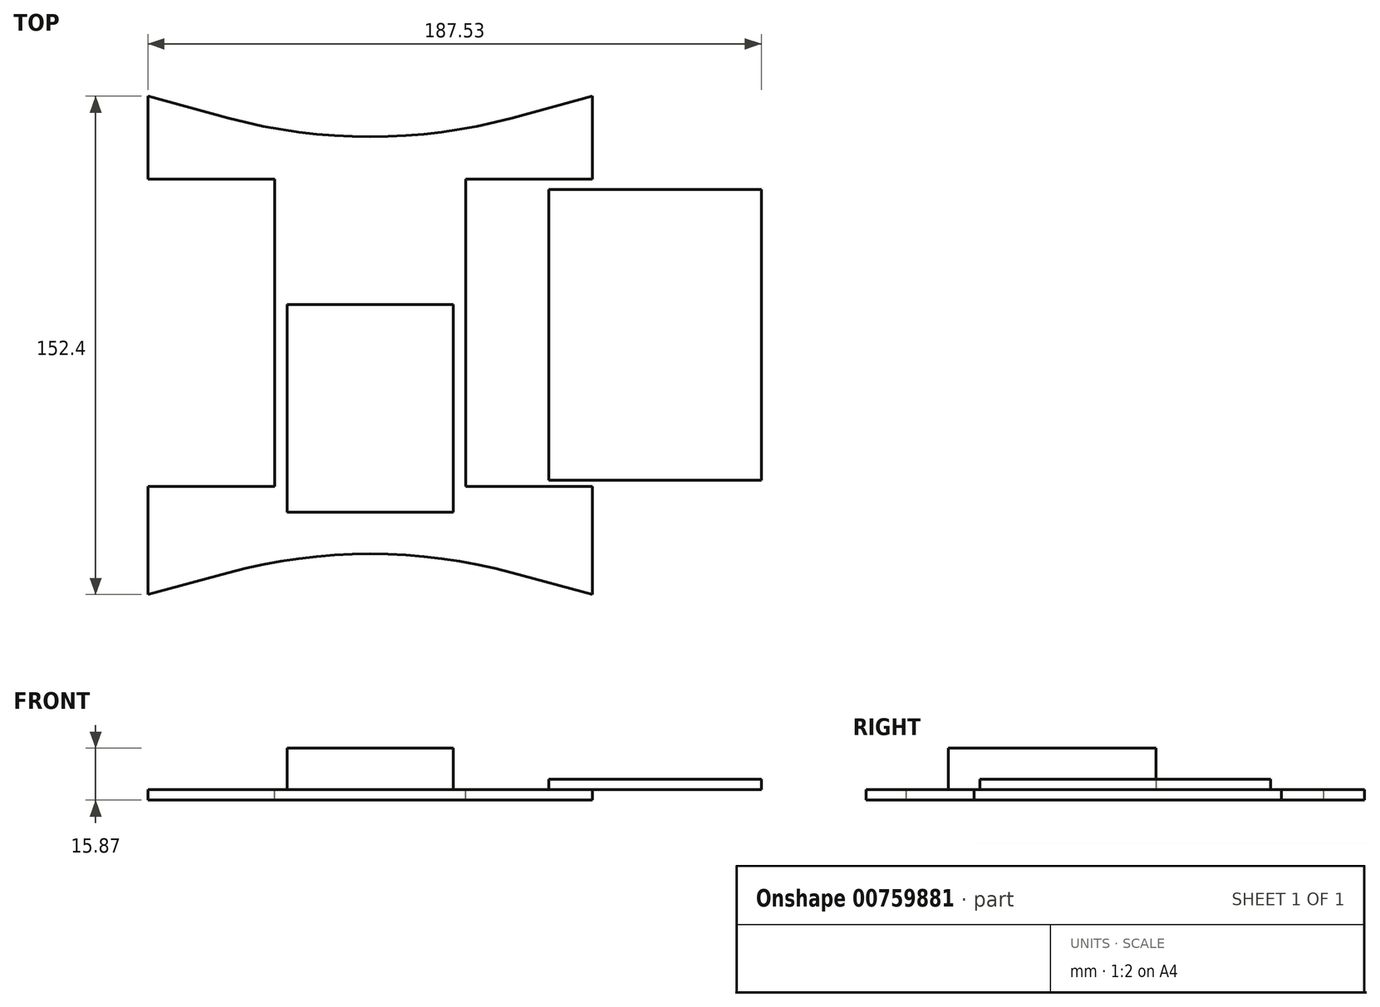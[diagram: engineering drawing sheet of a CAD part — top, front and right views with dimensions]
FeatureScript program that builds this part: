
annotation { "Feature Type Name" : "Feature", "Feature Type Description" : "" }
export const myFeature = defineFeature(function(context is Context, id is Id, definition is map)
    precondition{}
    {
        {
            var Q0;
            Q0=qCreatedBy(makeId("Top.planeOp"),FACE);
            var sketch = newSketch(context, id + "F0", { "sketchPlane" : qUnion([Q0])});
            skLineSegment(sketch, "E0.left", {"start": v(-67.95, 76.2) * mm, "end": v(-67.94, 50.8) * mm});
            skLineSegment(sketch, "E1", {"start": v(-67.94, 0) * mm, "end": v(67.94, 0) * mm});
            skLineSegment(sketch, "E2", {"start": v(-67.95, 76.2) * mm, "end": v(-43.43, 69.56) * mm});
            skArc(sketch, "E3.filletArc", {"start": v(-43.43, 69.56) * mm, "mid": v(-21.9, 65.23) * mm, "end": v(0, 63.77) * mm});
            skPoint(sketch, "E4.MirrorCS.end.orphan", {"position": v(-67.94, 0) * mm});
            skPoint(sketch, "E5", {"position": v(-67.94, 38.1) * mm});
            skPoint(sketch, "E6.MirrorP", {"position": v(67.94, 0) * mm});
            skPoint(sketch, "E7.MirrorP", {"position": v(67.94, 38.1) * mm});
            skLineSegment(sketch, "E8.MirrorCS", {"start": v(-67.95, -76.2) * mm, "end": v(-43.43, -69.56) * mm});
            skArc(sketch, "E9.MirrorCS", {"start": v(-43.43, -69.56) * mm, "mid": v(-21.9, -65.23) * mm, "end": v(0, -63.77) * mm});
            skLineSegment(sketch, "E10", {"start": v(-67.94, -43.18) * mm, "end": v(-67.95, -76.2) * mm});
            skLineSegment(sketch, "E11.bottom", {"start": v(-67.94, 50.8) * mm, "end": v(-29.2, 50.8) * mm});
            skLineSegment(sketch, "E11.top", {"start": v(-67.94, -43.18) * mm, "end": v(-29.2, -43.18) * mm});
            skLineSegment(sketch, "E11.right", {"start": v(-29.2, 50.8) * mm, "end": v(-29.2, 40.64) * mm});
            skPoint(sketch, "E12.firstSnap0", {"position": v(-59.18, 40.64) * mm});
            skLineSegment(sketch, "E13.trimOffspring", {"start": v(-29.2, 17.14) * mm, "end": v(-29.2, -43.18) * mm});
            skPoint(sketch, "E14.trimOffspring.start.orphan", {"position": v(-63.5, 14.6) * mm});
            skPoint(sketch, "E15.MirrorCS.end.orphan", {"position": v(0, 63.77) * mm});
            skPoint(sketch, "E15.MirrorCS.start.orphan", {"position": v(43.43, 69.56) * mm});
            skPoint(sketch, "E16.MirrorCS.start.orphan", {"position": v(67.95, 76.2) * mm});
            skPoint(sketch, "E17.MirrorCS.start.orphan", {"position": v(63.5, 14.6) * mm});
            skPoint(sketch, "E18.MirrorCS.end.orphan", {"position": v(0, -63.77) * mm});
            skPoint(sketch, "E18.MirrorCS.start.orphan", {"position": v(43.43, -69.56) * mm});
            skPoint(sketch, "E19.MirrorCS.start.orphan", {"position": v(67.95, -76.2) * mm});
            skLineSegment(sketch, "E20.MirrorCS", {"start": v(67.95, -76.2) * mm, "end": v(43.43, -69.56) * mm});
            skLineSegment(sketch, "E21.MirrorCS", {"start": v(67.95, 76.2) * mm, "end": v(67.94, 50.8) * mm});
            skPoint(sketch, "E22.MirrorP", {"position": v(59.18, 40.64) * mm});
            skLineSegment(sketch, "E23.MirrorCS", {"start": v(29.2, 50.8) * mm, "end": v(29.2, 40.64) * mm});
            skLineSegment(sketch, "E24.MirrorCS", {"start": v(67.94, -43.18) * mm, "end": v(29.2, -43.18) * mm});
            skLineSegment(sketch, "E25.MirrorCS", {"start": v(67.94, 50.8) * mm, "end": v(29.2, 50.8) * mm});
            skLineSegment(sketch, "E26.MirrorCS", {"start": v(67.94, -43.18) * mm, "end": v(67.95, -76.2) * mm});
            skArc(sketch, "E27.MirrorCS", {"start": v(43.43, -69.56) * mm, "mid": v(21.9, -65.23) * mm, "end": v(0, -63.77) * mm});
            skArc(sketch, "E28.MirrorCS", {"start": v(43.43, 69.56) * mm, "mid": v(21.9, 65.23) * mm, "end": v(0, 63.77) * mm});
            skLineSegment(sketch, "E29.MirrorCS", {"start": v(67.95, 76.2) * mm, "end": v(43.43, 69.56) * mm});
            skLineSegment(sketch, "E30.MirrorCS", {"start": v(29.2, 17.14) * mm, "end": v(29.2, -43.18) * mm});
            skLineSegment(sketch, "E31", {"start": v(-29.2, 17.14) * mm, "end": v(-29.2, 40.64) * mm});
            skPoint(sketch, "E12.right.end.orphan", {"position": v(-16.5, 17.14) * mm});
            skPoint(sketch, "E12.bottom.end.orphan", {"position": v(-16.5, 40.64) * mm});
            skLineSegment(sketch, "E32", {"start": v(29.2, 17.14) * mm, "end": v(29.2, 40.64) * mm});
            skPoint(sketch, "E33.MirrorCS.end.orphan", {"position": v(16.5, 17.14) * mm});
            skPoint(sketch, "E34.MirrorCS.end.orphan", {"position": v(16.5, 40.64) * mm});
            skSolve(sketch);
        }
        {
            var Q0;
            Q0=makeQuery(id+"F0.imprint","IMPRINT",FACE,{"disambiguationData":[TD([[makeQuery(id+"F0.imprint","IMPRINT",EDGE,{"derivedFrom":sQuery(id+"F0.wireOp",EDGE,"E1")}),-1.0]])]});
            var Q1;
            Q1=makeQuery(id+"F0.imprint","IMPRINT",FACE,{"disambiguationData":[TD([[makeQuery(id+"F0.imprint","IMPRINT",EDGE,{"derivedFrom":sQuery(id+"F0.wireOp",EDGE,"E0.left")}),1.0]])]});
            extrude(context, id + "F1", {"entities" : qUnion([Q0, Q1]), "oppositeDirection" : true, "depth" : 3.17 * mm, "offsetDistance" : 25.4 * mm});
        }
        {
            var Q0;
            Q0=makeQuery(id+"F1.opExtrude","CAP_FACE",FACE,{"disambiguationData":[OSD([sQuery(id+"F0.wireOp",EDGE,"E0.left"),sQuery(id+"F0.wireOp",EDGE,"E0.right"),sQuery(id+"F0.wireOp",EDGE,"E2"),sQuery(id+"F0.wireOp",EDGE,"nF0zVBHC-JgX4-6R4l-cEPk-SVyycXWpVrUL"),sQuery(id+"F0.wireOp",EDGE,"E3.filletArc"),sQuery(id+"F0.wireOp",EDGE,"E4.MirrorCS"),sQuery(id+"F0.wireOp",EDGE,"f067e53b-9093-44e8-8a77-9cfb6b69a42c0.MirrorCS"),sQuery(id+"F0.wireOp",EDGE,"ce7b3c39-1281-45ce-9da9-329222d67ca30.MirrorCS"),sQuery(id+"F0.wireOp",EDGE,"57a77b3d-40ae-4a20-83b1-77d539f986f80.MirrorCS"),sQuery(id+"F0.wireOp",EDGE,"7563793e-4717-4190-b109-ab0f6ad7fca70.MirrorCS")])],"isStart":true});
            var sketch = newSketch(context, id + "F2", { "sketchPlane" : qUnion([Q0])});
            skLineSegment(sketch, "E35.bottom", {"start": v(-25.4, -51) * mm, "end": v(25.4, -51) * mm});
            skLineSegment(sketch, "E35.top", {"start": v(-25.4, 12.5) * mm, "end": v(25.4, 12.5) * mm});
            skLineSegment(sketch, "E35.left", {"start": v(-25.4, -51) * mm, "end": v(-25.4, 12.5) * mm});
            skLineSegment(sketch, "E35.right", {"start": v(25.4, -51) * mm, "end": v(25.4, 12.5) * mm});
            skSolve(sketch);
        }
        {
            var Q0;
            Q0=makeQuery(id+"F2.imprint","IMPRINT",FACE,{"disambiguationData":[TD([[makeQuery(id+"F2.imprint","IMPRINT",EDGE,{"derivedFrom":sQuery(id+"F2.wireOp",EDGE,"E35.bottom")}),1.0]])]});
            extrude(context, id + "F3", {"entities" : qUnion([Q0]), "depth" : 12.7 * mm, "offsetDistance" : 25.4 * mm});
        }
        {
            var Q0;
            Q0=qCreatedBy(makeId("Top.planeOp"),FACE);
            var sketch = newSketch(context, id + "F4", { "sketchPlane" : qUnion([Q0])});
            skLineSegment(sketch, "E36.bottom", {"start": v(54.56, 47.61) * mm, "end": v(119.58, 47.61) * mm});
            skLineSegment(sketch, "E36.top", {"start": v(54.56, -41.29) * mm, "end": v(119.58, -41.29) * mm});
            skLineSegment(sketch, "E36.left", {"start": v(54.56, 47.61) * mm, "end": v(54.56, -41.29) * mm});
            skLineSegment(sketch, "E36.right", {"start": v(119.58, 47.61) * mm, "end": v(119.58, -41.29) * mm});
            skSolve(sketch);
        }
        {
            var Q0;
            Q0=makeQuery(id+"F4.imprint","IMPRINT",FACE,{"disambiguationData":[TD([[makeQuery(id+"F4.imprint","IMPRINT",EDGE,{"derivedFrom":sQuery(id+"F4.wireOp",EDGE,"E36.bottom")}),-1.0]])]});
            extrude(context, id + "F5", {"entities" : qUnion([Q0]), "depth" : 3.17 * mm, "offsetDistance" : 25.4 * mm});
        }
    });
